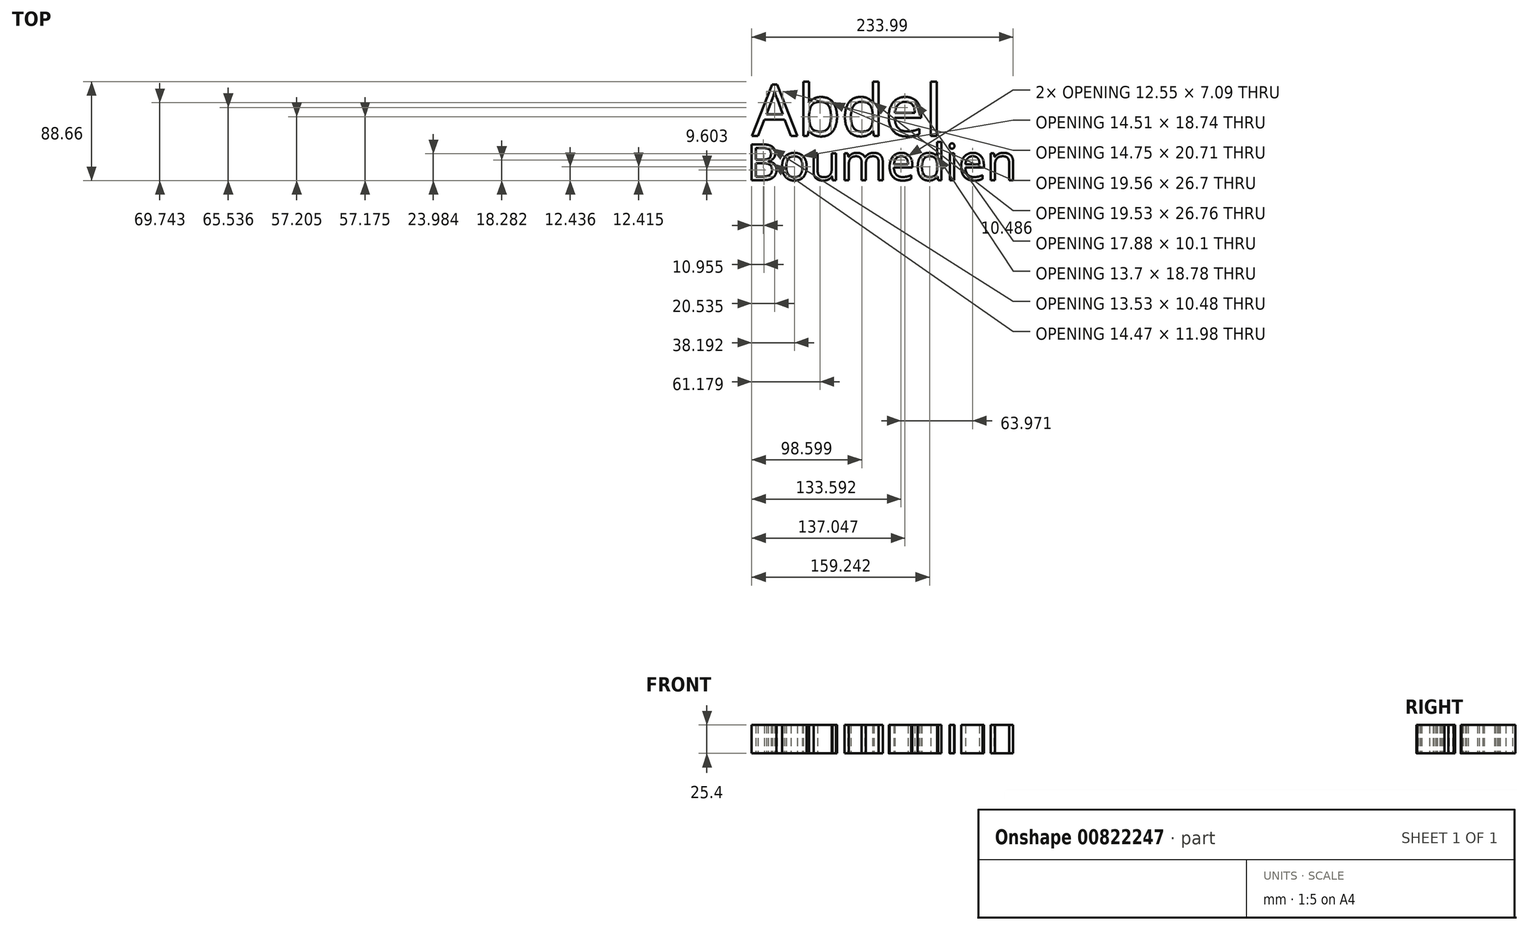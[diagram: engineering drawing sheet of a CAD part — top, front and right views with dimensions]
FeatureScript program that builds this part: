
annotation { "Feature Type Name" : "Feature", "Feature Type Description" : "" }
export const myFeature = defineFeature(function(context is Context, id is Id, definition is map)
    precondition{}
    {
        {
            var Q0;
            Q0=qCreatedBy(makeId("Top.planeOp"),FACE);
            var sketch = newSketch(context, id + "F0", { "sketchPlane" : qUnion([Q0])});
            skText(sketch, "E0", { "text": "Abdel\n", "fontName": "OpenSans-Regular.ttf"});
            skText(sketch, "E1", { "text": "Boumedien\n", "fontName": "OpenSans-Regular.ttf"});
            const initialGuessF0  = {"E0": [-0.11628, -0.01026, 1, 0, 0.046], "E1": [-0.12098, -0.04993, 1, 0, 0.03228]};
            skSetInitialGuess(sketch, initialGuessF0);
            skSolve(sketch);
        }
        {
            var Q0;
            Q0 = qSketchRegion(id + "F0", true);
            extrude(context, id + "F1", {"entities" : qUnion([Q0]), "depth" : 25.4 * mm, "offsetDistance" : 25.4 * mm});
        }
    });
